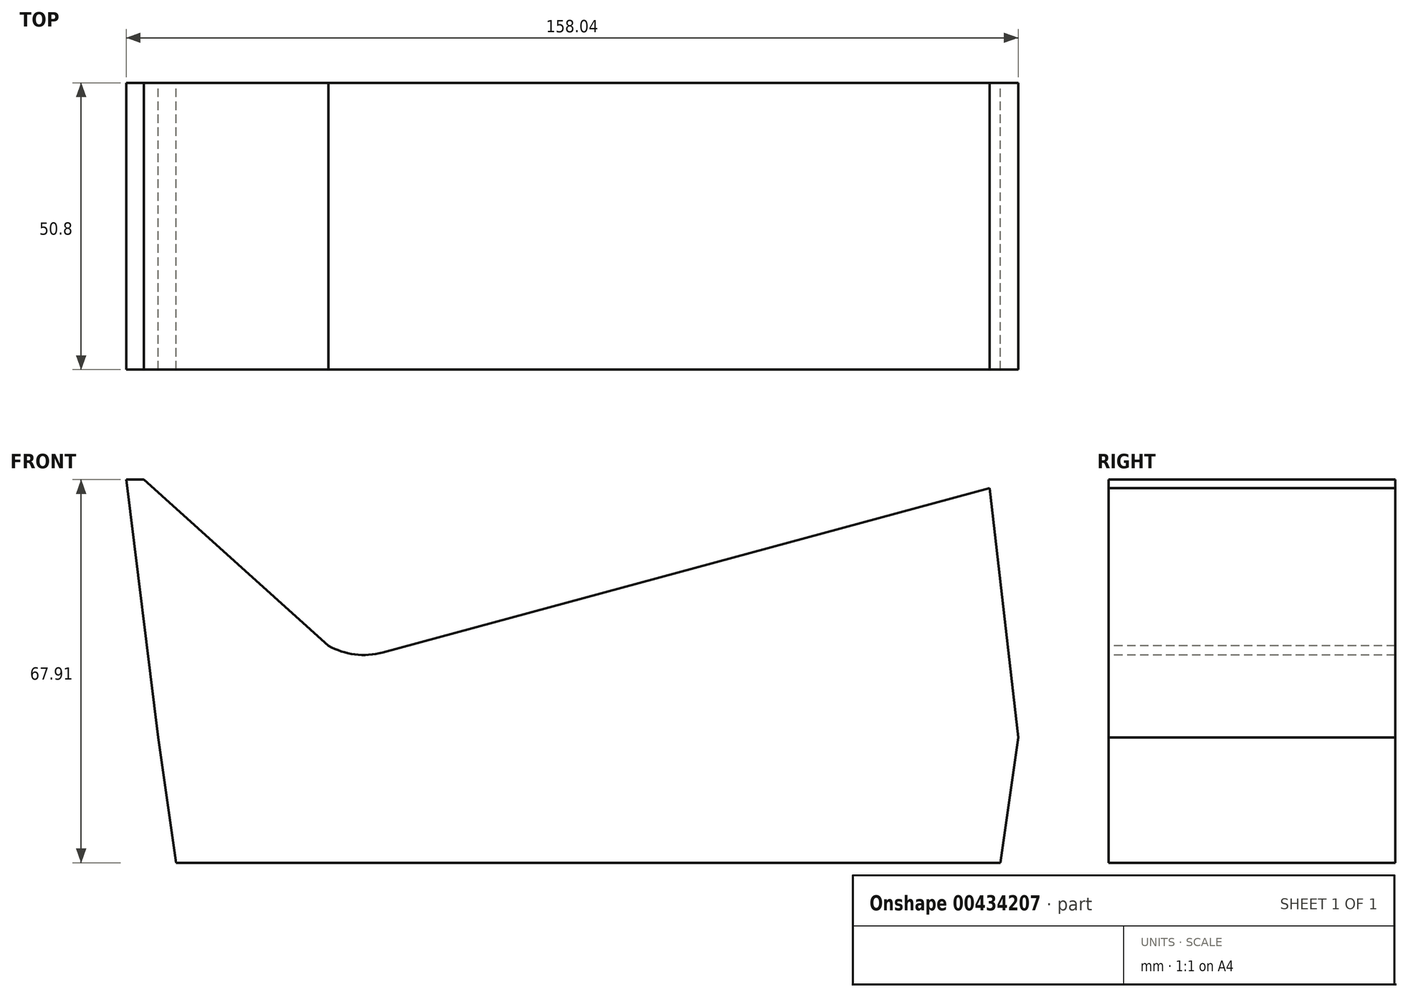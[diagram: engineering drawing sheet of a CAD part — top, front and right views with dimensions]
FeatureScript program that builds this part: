
annotation { "Feature Type Name" : "Feature", "Feature Type Description" : "" }
export const myFeature = defineFeature(function(context is Context, id is Id, definition is map)
    precondition{}
    {
        {
            var Q0;
            Q0=qCreatedBy(makeId("Front.planeOp"),FACE);
            var sketch = newSketch(context, id + "F0", { "sketchPlane" : qUnion([Q0])});
            skLineSegment(sketch, "E0", {"start": v(-69.72, -6.03) * mm, "end": v(82.68, -6.03) * mm});
            skLineSegment(sketch, "E1", {"start": v(6.48, -28.25) * mm, "end": v(-66.54, -28.25) * mm});
            skLineSegment(sketch, "E2", {"start": v(6.48, -28.25) * mm, "end": v(79.5, -28.25) * mm});
            skLineSegment(sketch, "E3", {"start": v(-69.72, -6.03) * mm, "end": v(-66.54, -28.25) * mm});
            skLineSegment(sketch, "E4", {"start": v(82.68, -6.03) * mm, "end": v(79.5, -28.25) * mm});
            skSolve(sketch);
        }
        {
            var Q0;
            Q0=makeQuery(id+"F0.imprint","IMPRINT",FACE,{"disambiguationData":[TD([[makeQuery(id+"F0.imprint","IMPRINT",EDGE,{"derivedFrom":sQuery(id+"F0.wireOp",EDGE,"E0")}),-1.0]])]});
            extrude(context, id + "F1", {"entities" : qUnion([Q0]), "depth" : 50.8 * mm});
        }
        {
            var Q0;
            Q0=makeQuery(id+"F1.opExtrude","CAP_FACE",FACE,{"disambiguationData":[OSD([sQuery(id+"F0.wireOp",EDGE,"E0"),sQuery(id+"F0.wireOp",EDGE,"E1"),sQuery(id+"F0.wireOp",EDGE,"E2"),sQuery(id+"F0.wireOp",EDGE,"E3"),sQuery(id+"F0.wireOp",EDGE,"E4")])],"isStart":false});
            var sketch = newSketch(context, id + "F2", { "sketchPlane" : qUnion([Q0])});
            skLineSegment(sketch, "E5", {"start": v(82.68, -6.03) * mm, "end": v(77.63, 38.14) * mm});
            skLineSegment(sketch, "E6", {"start": v(-69.72, -6.03) * mm, "end": v(-75.36, 39.66) * mm});
            skLineSegment(sketch, "E7", {"start": v(-29.96, 9.01) * mm, "end": v(77.63, 38.14) * mm});
            skPoint(sketch, "E8.visualSharp", {"position": v(-34.83, 7.7) * mm});
            skArc(sketch, "E8.filletArc", {"start": v(-39.51, 10.2) * mm, "mid": v(-34.85, 8.67) * mm, "end": v(-29.96, 9.01) * mm});
            skLineSegment(sketch, "E9", {"start": v(-75.36, 39.66) * mm, "end": v(-72.23, 39.66) * mm});
            skLineSegment(sketch, "E10", {"start": v(-72.23, 39.66) * mm, "end": v(-39.51, 10.2) * mm});
            skSolve(sketch);
        }
        {
            var Q0;
            Q0=makeQuery(id+"F2.imprint","IMPRINT",FACE,{"disambiguationData":[TD([[makeQuery(id+"F2.imprint","IMPRINT",EDGE,{"derivedFrom":sQuery(id+"F2.wireOp",EDGE,"E5")}),1.0]])]});
            extrude(context, id + "F3", {"entities" : qUnion([Q0]), "operationType" : NewBodyOperationType.ADD, "oppositeDirection" : true, "depth" : 50.8 * mm});
        }
    });
